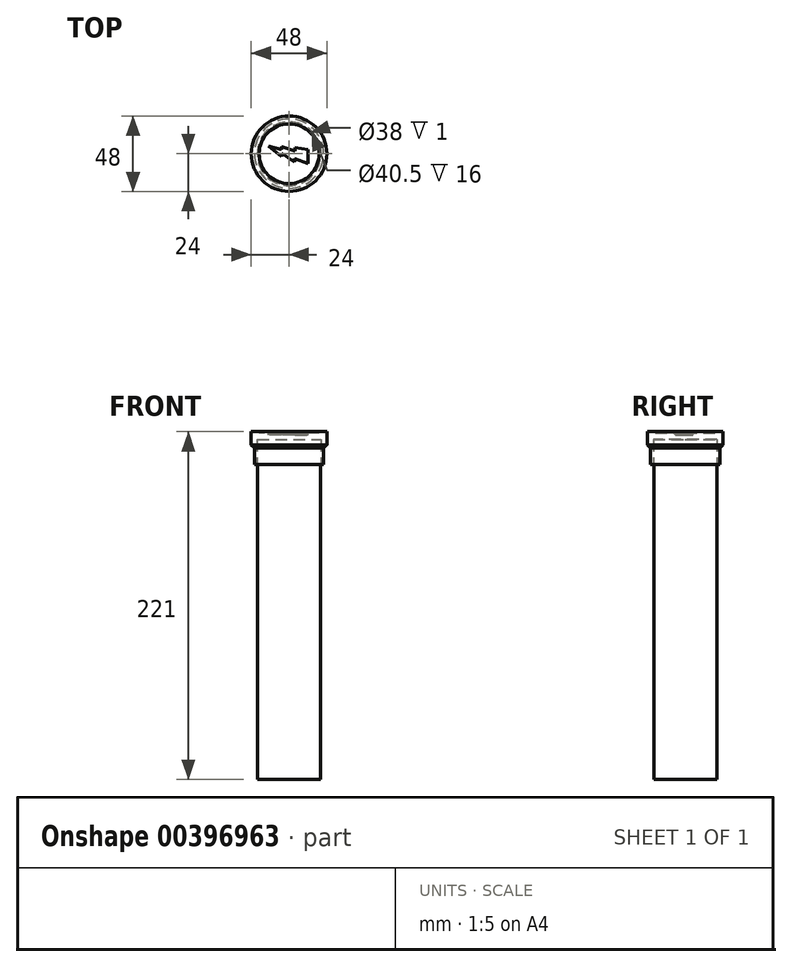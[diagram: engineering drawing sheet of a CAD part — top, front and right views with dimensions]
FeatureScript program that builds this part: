
annotation { "Feature Type Name" : "Feature", "Feature Type Description" : "" }
export const myFeature = defineFeature(function(context is Context, id is Id, definition is map)
    precondition{}
    {
        {
            var Q0;
            Q0=qCreatedBy(makeId("Front.planeOp"),FACE);
            var sketch = newSketch(context, id + "F0", { "sketchPlane" : qUnion([Q0])});
            skLineSegment(sketch, "E0", {"start": v(-20, 0) * mm, "end": v(-22, 0) * mm});
            skLineSegment(sketch, "E1", {"start": v(0, 0) * mm, "end": v(-20, 0) * mm});
            skLineSegment(sketch, "E2", {"start": v(-22, 0) * mm, "end": v(-22, 15.51) * mm});
            skLineSegment(sketch, "E3", {"start": v(-22, 20) * mm, "end": v(0, 20) * mm});
            skLineSegment(sketch, "E4", {"start": v(0, 20) * mm, "end": v(0, 0) * mm});
            skLineSegment(sketch, "E5", {"start": v(-22, 20) * mm, "end": v(-24, 20) * mm});
            skLineSegment(sketch, "E6", {"start": v(-24, 20) * mm, "end": v(-24, 15.51) * mm});
            skLineSegment(sketch, "E7", {"start": v(-24, 15.51) * mm, "end": v(-22, 15.51) * mm});
            skSolve(sketch);
        }
        {
            var Q0;
            Q0=makeQuery(id+"F0.imprint","IMPRINT",FACE,{"disambiguationData":[TD([[makeQuery(id+"F0.imprint","IMPRINT",EDGE,{"derivedFrom":sQuery(id+"F0.wireOp",EDGE,"E0")}),-1.0]])]});
            var Q1;
            Q1=sQuery(id+"F0.wireOp",EDGE,"E4");
            revolve(context, id + "F1", {"entities" : qUnion([Q0]), "axis" : qUnion([Q1]), "revolveType" : RevolveType.FULL});
        }
        {
            var Q0;
            Q0=qCreatedBy(makeId("Top.planeOp"),FACE);
            var sketch = newSketch(context, id + "F2", { "sketchPlane" : qUnion([Q0])});
            skCircle(sketch, "E8", {"center": v(0, 0) * mm, "radius": 20 * mm});
            skSolve(sketch);
        }
        {
            var Q0;
            Q0=makeQuery(id+"F2.imprint","IMPRINT",FACE,{"disambiguationData":[TD([[makeQuery(id+"F2.imprint","IMPRINT",EDGE,{"derivedFrom":sQuery(id+"F2.wireOp",EDGE,"E8")}),1.0]])]});
            extrude(context, id + "F3", {"entities" : qUnion([Q0]), "oppositeDirection" : true, "depth" : 200 * mm});
        }
        {
            var Q0;
            Q0=makeQuery(id+"F1.opRevolve","SWEPT_FACE",FACE,{"disambiguationData":[OSD([sQuery(id+"F0.wireOp",EDGE,"E3")])]});
            var sketch = newSketch(context, id + "F4", { "sketchPlane" : qUnion([Q0])});
            skSolve(sketch);
        }
        {
            var Q0;
            Q0=makeQuery(id+"F4.imprint","IMPRINT",FACE,{"disambiguationData":[TD([[makeQuery(id+"F4.imprint","IMPRINT",EDGE,{"derivedFrom":makeQuery(id+"F1.opRevolve","SWEPT_EDGE",EDGE,{"disambiguationData":[OSD([sQuery(id+"F0.wireOp",EDGE,"E5"),sQuery(id+"F0.wireOp",EDGE,"E6")])]})}),1.0]])]});
            var sketch = newSketch(context, id + "F5", { "sketchPlane" : qUnion([Q0])});
            skLineSegment(sketch, "E9", {"start": v(11.98, 2.6) * mm, "end": v(11.98, -6.22) * mm});
            skLineSegment(sketch, "E10", {"start": v(11.98, -6.22) * mm, "end": v(3.47, -2.97) * mm});
            skLineSegment(sketch, "E11", {"start": v(3.47, -2.97) * mm, "end": v(3.47, -5.17) * mm});
            skLineSegment(sketch, "E12", {"start": v(3.47, -5.17) * mm, "end": v(-4.66, 0.38) * mm});
            skLineSegment(sketch, "E13", {"start": v(-4.66, 0.38) * mm, "end": v(-4.66, -1.83) * mm});
            skLineSegment(sketch, "E14", {"start": v(-4.66, -1.83) * mm, "end": v(-13.02, 4.8) * mm});
            skLineSegment(sketch, "E15", {"start": v(3.89, 1.57) * mm, "end": v(3.89, 3.86) * mm});
            skLineSegment(sketch, "E16", {"start": v(3.89, 3.86) * mm, "end": v(11.98, 2.6) * mm});
            skLineSegment(sketch, "E17", {"start": v(3.89, 1.57) * mm, "end": v(-4.83, 4.5) * mm});
            skLineSegment(sketch, "E18", {"start": v(-4.83, 4.5) * mm, "end": v(-4.83, 2.7) * mm});
            skLineSegment(sketch, "E19", {"start": v(-4.83, 2.7) * mm, "end": v(-13.02, 4.8) * mm});
            skCircle(sketch, "E20", {"center": v(0, 0) * mm, "radius": 19 * mm});
            skSolve(sketch);
        }
        {
            var Q0;
            Q0=makeQuery(id+"F5.imprint","IMPRINT",FACE,{"disambiguationData":[TD([[makeQuery(id+"F5.imprint","IMPRINT",EDGE,{"derivedFrom":sQuery(id+"F5.wireOp",EDGE,"E9")}),-1.0]])]});
            extrude(context, id + "F6", {"entities" : qUnion([Q0]), "operationType" : NewBodyOperationType.REMOVE, "oppositeDirection" : true, "depth" : 1 * mm});
        }
        {
            var Q0;
            Q0=makeQuery(id+"F5.imprint","IMPRINT",FACE,{"disambiguationData":[TD([[makeQuery(id+"F5.imprint","IMPRINT",EDGE,{"derivedFrom":sQuery(id+"F5.wireOp",EDGE,"E20")}),-1.0]])]});
            extrude(context, id + "F7", {"entities" : qUnion([Q0]), "operationType" : NewBodyOperationType.ADD, "depth" : 1 * mm});
        }
        {
            var Q0;
            Q0=makeQuery(id+"F1.opRevolve","SWEPT_FACE",FACE,{"disambiguationData":[OSD([sQuery(id+"F0.wireOp",EDGE,"E0"),sQuery(id+"F0.wireOp",EDGE,"E1")])]});
            var sketch = newSketch(context, id + "F8", { "sketchPlane" : qUnion([Q0])});
            skCircle(sketch, "E21", {"center": v(0, 0) * mm, "radius": 20.25 * mm});
            skSolve(sketch);
        }
        {
            var Q0;
            Q0=makeQuery(id+"F8.imprint","IMPRINT",FACE,{"disambiguationData":[TD([[makeQuery(id+"F8.imprint","IMPRINT",EDGE,{"derivedFrom":sQuery(id+"F8.wireOp",EDGE,"E21")}),1.0]])]});
            extrude(context, id + "F9", {"entities" : qUnion([Q0]), "operationType" : NewBodyOperationType.REMOVE, "oppositeDirection" : true, "depth" : 16 * mm});
        }
        {
            var Q0;
            Q0=makeQuery(id+"F1.opRevolve","SWEPT_EDGE",EDGE,{"disambiguationData":[OSD([sQuery(id+"F0.wireOp",EDGE,"E2"),sQuery(id+"F0.wireOp",EDGE,"E7")])]});
            chamfer(context, id + "F10", {"entities" : qUnion([Q0]), "width" : 5 * mm, "tangentPropagation" : true});
        }
    });
